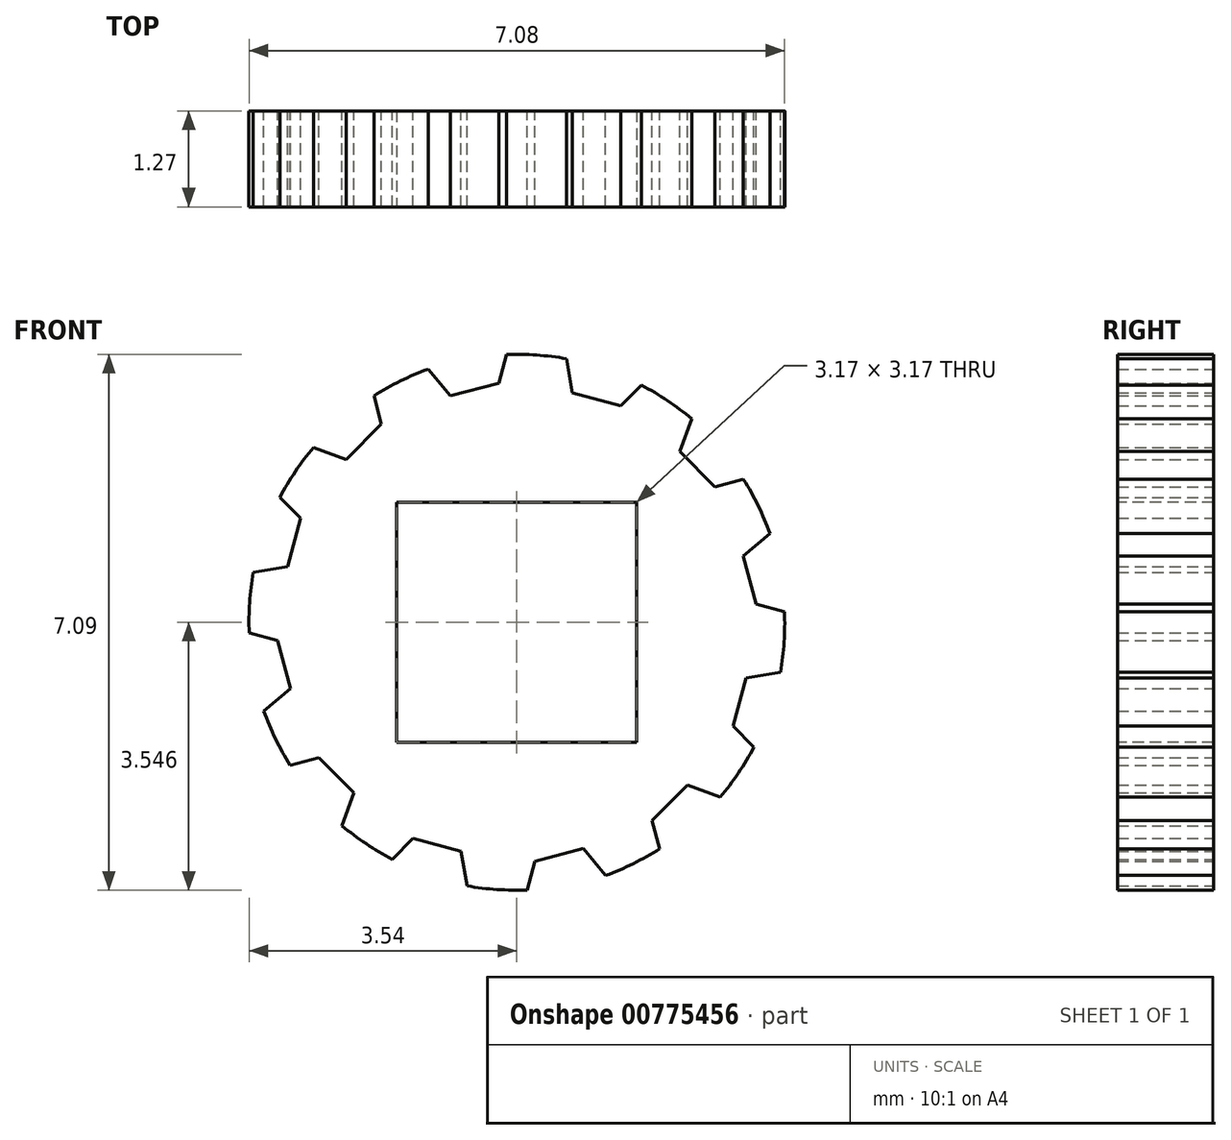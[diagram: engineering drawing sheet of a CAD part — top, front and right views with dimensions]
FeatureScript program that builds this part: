
annotation { "Feature Type Name" : "Feature", "Feature Type Description" : "" }
export const myFeature = defineFeature(function(context is Context, id is Id, definition is map)
    precondition{}
    {
        {
            var Q0;
            Q0=qCreatedBy(makeId("Front.planeOp"),FACE);
            var sketch = newSketch(context, id + "F0", { "sketchPlane" : qUnion([Q0])});
            skCircle(sketch, "E0", {"center": v(0, 0) * mm, "radius": 3.81 * mm});
            skLineSegment(sketch, "E1", {"start": v(3.81, 0) * mm, "end": v(3.81, -2.14) * mm});
            skLineSegment(sketch, "E2", {"start": v(3.81, 0) * mm, "end": v(3.81, 1.7) * mm});
            skLineSegment(sketch, "E3", {"start": v(3.81, -2.14) * mm, "end": v(3.81, 1.7) * mm});
            skLineSegment(sketch, "E4", {"start": v(0, 0) * mm, "end": v(4.56, 1.22) * mm});
            skLineSegment(sketch, "E5", {"start": v(0, 0) * mm, "end": v(5.89, -1.58) * mm});
            skLineSegment(sketch, "E6", {"start": v(0, 0) * mm, "end": v(6.8, 0.6) * mm});
            skLineSegment(sketch, "E7", {"start": v(0, 0) * mm, "end": v(7.02, -0.61) * mm});
            skLineSegment(sketch, "E8", {"start": v(3.81, 0.33) * mm, "end": v(4.14, 0.33) * mm});
            skLineSegment(sketch, "E9", {"start": v(3.81, -0.33) * mm, "end": v(4.23, -0.33) * mm});
            skLineSegment(sketch, "E10", {"start": v(3.08, 0.83) * mm, "end": v(3.16, 0.5) * mm});
            skLineSegment(sketch, "E11", {"start": v(3.08, 0.83) * mm, "end": v(3, 1.14) * mm});
            skLineSegment(sketch, "E12", {"start": v(3.16, 0.5) * mm, "end": v(3.81, 0.33) * mm});
            skLineSegment(sketch, "E13", {"start": v(3, 1.14) * mm, "end": v(3.6, 1.65) * mm});
            skLineSegment(sketch, "E14", {"start": v(3.81, 0.33) * mm, "end": v(3.6, 1.65) * mm});
            skLineSegment(sketch, "E15.1.0", {"start": v(2.15, 2.52) * mm, "end": v(2.43, 3.26) * mm});
            skLineSegment(sketch, "E15.1.1", {"start": v(3.27, 2.23) * mm, "end": v(2.43, 3.26) * mm});
            skLineSegment(sketch, "E15.1.2", {"start": v(2.39, 2.29) * mm, "end": v(2.15, 2.52) * mm});
            skLineSegment(sketch, "E15.1.3", {"start": v(2.39, 2.29) * mm, "end": v(2.62, 2.06) * mm});
            skLineSegment(sketch, "E15.1.4", {"start": v(2.62, 2.06) * mm, "end": v(3.27, 2.23) * mm});
            skCircle(sketch, "E15.1.5", {"center": v(0.13, 0.04) * mm, "radius": 3.81 * mm});
            skLineSegment(sketch, "E15.2.0", {"start": v(0.74, 3.3) * mm, "end": v(0.6, 4.07) * mm});
            skLineSegment(sketch, "E15.2.1", {"start": v(1.85, 3.6) * mm, "end": v(0.6, 4.07) * mm});
            skLineSegment(sketch, "E15.2.2", {"start": v(1.06, 3.21) * mm, "end": v(0.74, 3.3) * mm});
            skLineSegment(sketch, "E15.2.3", {"start": v(1.06, 3.21) * mm, "end": v(1.37, 3.13) * mm});
            skLineSegment(sketch, "E15.2.4", {"start": v(1.37, 3.13) * mm, "end": v(1.85, 3.6) * mm});
            skCircle(sketch, "E15.2.5", {"center": v(0.23, 0.13) * mm, "radius": 3.81 * mm});
            skLineSegment(sketch, "E15.3.0", {"start": v(-0.88, 3.26) * mm, "end": v(-1.38, 3.86) * mm});
            skLineSegment(sketch, "E15.3.1", {"start": v(-0.07, 4.08) * mm, "end": v(-1.38, 3.86) * mm});
            skLineSegment(sketch, "E15.3.2", {"start": v(-0.56, 3.35) * mm, "end": v(-0.88, 3.26) * mm});
            skLineSegment(sketch, "E15.3.3", {"start": v(-0.56, 3.35) * mm, "end": v(-0.24, 3.43) * mm});
            skLineSegment(sketch, "E15.3.4", {"start": v(-0.24, 3.43) * mm, "end": v(-0.07, 4.08) * mm});
            skCircle(sketch, "E15.3.5", {"center": v(0.27, 0.27) * mm, "radius": 3.81 * mm});
            skLineSegment(sketch, "E15.4.0", {"start": v(-2.26, 2.42) * mm, "end": v(-3, 2.7) * mm});
            skLineSegment(sketch, "E15.4.1", {"start": v(-1.96, 3.53) * mm, "end": v(-3, 2.7) * mm});
            skLineSegment(sketch, "E15.4.2", {"start": v(-2.02, 2.65) * mm, "end": v(-2.26, 2.42) * mm});
            skLineSegment(sketch, "E15.4.3", {"start": v(-2.02, 2.65) * mm, "end": v(-1.8, 2.89) * mm});
            skLineSegment(sketch, "E15.4.4", {"start": v(-1.8, 2.89) * mm, "end": v(-1.96, 3.53) * mm});
            skCircle(sketch, "E15.4.5", {"center": v(0.23, 0.4) * mm, "radius": 3.81 * mm});
            skLineSegment(sketch, "E15.5.0", {"start": v(-3.03, 1) * mm, "end": v(-3.8, 0.87) * mm});
            skLineSegment(sketch, "E15.5.1", {"start": v(-3.33, 2.11) * mm, "end": v(-3.8, 0.87) * mm});
            skLineSegment(sketch, "E15.5.2", {"start": v(-2.95, 1.32) * mm, "end": v(-3.03, 1) * mm});
            skLineSegment(sketch, "E15.5.3", {"start": v(-2.95, 1.32) * mm, "end": v(-2.86, 1.64) * mm});
            skLineSegment(sketch, "E15.5.4", {"start": v(-2.86, 1.64) * mm, "end": v(-3.33, 2.11) * mm});
            skCircle(sketch, "E15.5.5", {"center": v(0.13, 0.5) * mm, "radius": 3.81 * mm});
            skLineSegment(sketch, "E15.6.0", {"start": v(-3, -0.61) * mm, "end": v(-3.6, -1.11) * mm});
            skLineSegment(sketch, "E15.6.1", {"start": v(-3.81, 0.2) * mm, "end": v(-3.6, -1.11) * mm});
            skLineSegment(sketch, "E15.6.2", {"start": v(-3.08, -0.3) * mm, "end": v(-3, -0.61) * mm});
            skLineSegment(sketch, "E15.6.3", {"start": v(-3.08, -0.3) * mm, "end": v(-3.16, 0.03) * mm});
            skLineSegment(sketch, "E15.6.4", {"start": v(-3.16, 0.03) * mm, "end": v(-3.81, 0.2) * mm});
            skCircle(sketch, "E15.6.5", {"center": v(0, 0.53) * mm, "radius": 3.81 * mm});
            skLineSegment(sketch, "E15.7.0", {"start": v(-2.15, -2) * mm, "end": v(-2.43, -2.73) * mm});
            skLineSegment(sketch, "E15.7.1", {"start": v(-3.27, -1.7) * mm, "end": v(-2.43, -2.73) * mm});
            skLineSegment(sketch, "E15.7.2", {"start": v(-2.39, -1.76) * mm, "end": v(-2.15, -2) * mm});
            skLineSegment(sketch, "E15.7.3", {"start": v(-2.39, -1.76) * mm, "end": v(-2.62, -1.52) * mm});
            skLineSegment(sketch, "E15.7.4", {"start": v(-2.62, -1.52) * mm, "end": v(-3.27, -1.7) * mm});
            skCircle(sketch, "E15.7.5", {"center": v(-0.13, 0.5) * mm, "radius": 3.81 * mm});
            skLineSegment(sketch, "E15.8.0", {"start": v(-0.74, -2.77) * mm, "end": v(-0.6, -3.54) * mm});
            skLineSegment(sketch, "E15.8.1", {"start": v(-1.85, -3.07) * mm, "end": v(-0.6, -3.54) * mm});
            skLineSegment(sketch, "E15.8.2", {"start": v(-1.06, -2.68) * mm, "end": v(-0.74, -2.77) * mm});
            skLineSegment(sketch, "E15.8.3", {"start": v(-1.06, -2.68) * mm, "end": v(-1.37, -2.6) * mm});
            skLineSegment(sketch, "E15.8.4", {"start": v(-1.37, -2.6) * mm, "end": v(-1.85, -3.07) * mm});
            skCircle(sketch, "E15.8.5", {"center": v(-0.23, 0.4) * mm, "radius": 3.81 * mm});
            skLineSegment(sketch, "E15.9.0", {"start": v(0.88, -2.73) * mm, "end": v(1.38, -3.33) * mm});
            skLineSegment(sketch, "E15.9.1", {"start": v(0.07, -3.54) * mm, "end": v(1.38, -3.33) * mm});
            skLineSegment(sketch, "E15.9.2", {"start": v(0.56, -2.81) * mm, "end": v(0.88, -2.73) * mm});
            skLineSegment(sketch, "E15.9.3", {"start": v(0.56, -2.81) * mm, "end": v(0.24, -2.9) * mm});
            skLineSegment(sketch, "E15.9.4", {"start": v(0.24, -2.9) * mm, "end": v(0.07, -3.54) * mm});
            skCircle(sketch, "E15.9.5", {"center": v(-0.27, 0.27) * mm, "radius": 3.81 * mm});
            skLineSegment(sketch, "E15.10.0", {"start": v(2.26, -1.89) * mm, "end": v(3, -2.16) * mm});
            skLineSegment(sketch, "E15.10.1", {"start": v(1.96, -3) * mm, "end": v(3, -2.16) * mm});
            skLineSegment(sketch, "E15.10.2", {"start": v(2.02, -2.12) * mm, "end": v(2.26, -1.89) * mm});
            skLineSegment(sketch, "E15.10.3", {"start": v(2.02, -2.12) * mm, "end": v(1.8, -2.35) * mm});
            skLineSegment(sketch, "E15.10.4", {"start": v(1.8, -2.35) * mm, "end": v(1.96, -3) * mm});
            skCircle(sketch, "E15.10.5", {"center": v(-0.23, 0.13) * mm, "radius": 3.81 * mm});
            skLineSegment(sketch, "E15.11.0", {"start": v(3.03, -0.47) * mm, "end": v(3.8, -0.34) * mm});
            skLineSegment(sketch, "E15.11.1", {"start": v(3.33, -1.58) * mm, "end": v(3.8, -0.34) * mm});
            skLineSegment(sketch, "E15.11.2", {"start": v(2.95, -0.79) * mm, "end": v(3.03, -0.47) * mm});
            skLineSegment(sketch, "E15.11.3", {"start": v(2.95, -0.79) * mm, "end": v(2.86, -1.1) * mm});
            skLineSegment(sketch, "E15.11.4", {"start": v(2.86, -1.1) * mm, "end": v(3.33, -1.58) * mm});
            skCircle(sketch, "E15.11.5", {"center": v(-0.13, 0.04) * mm, "radius": 3.81 * mm});
            skPoint(sketch, "E15.center", {"position": v(0, 0.27) * mm});
            skLineSegment(sketch, "E16", {"start": v(3.27, 2.23) * mm, "end": v(3.6, 1.65) * mm});
            skLineSegment(sketch, "E17", {"start": v(1.85, 3.6) * mm, "end": v(2.43, 3.26) * mm});
            skLineSegment(sketch, "E18", {"start": v(-1.38, 3.86) * mm, "end": v(-0.07, 4.08) * mm});
            skLineSegment(sketch, "E19", {"start": v(-1.96, 3.53) * mm, "end": v(-1.38, 3.86) * mm});
            skLineSegment(sketch, "E20", {"start": v(-0.07, 4.08) * mm, "end": v(0.6, 4.07) * mm});
            skLineSegment(sketch, "E21", {"start": v(-3, 2.7) * mm, "end": v(-3.33, 2.11) * mm});
            skLineSegment(sketch, "E22", {"start": v(-3.8, 0.87) * mm, "end": v(-3.81, 0.2) * mm});
            skLineSegment(sketch, "E23", {"start": v(-3.6, -1.11) * mm, "end": v(-3.27, -1.7) * mm});
            skLineSegment(sketch, "E24", {"start": v(-2.43, -2.73) * mm, "end": v(-1.85, -3.07) * mm});
            skLineSegment(sketch, "E25", {"start": v(-0.6, -3.54) * mm, "end": v(0.07, -3.54) * mm});
            skLineSegment(sketch, "E26", {"start": v(1.38, -3.33) * mm, "end": v(1.96, -3) * mm});
            skLineSegment(sketch, "E27", {"start": v(3, -2.16) * mm, "end": v(3.33, -1.58) * mm});
            skLineSegment(sketch, "E28", {"start": v(3.8, -0.34) * mm, "end": v(3.81, 0.33) * mm});
            skSolve(sketch);
        }
        {
            var Q0;
            {var subQ49=sQuery(id+"F0.wireOp",EDGE,"E11");Q0=makeQuery(id+"F0.imprint","IMPRINT",FACE,{"disambiguationData":[TD([[makeQuery(id+"F0.imprint","IMPRINT",EDGE,{"derivedFrom":subQ49}),1.0]])]});}
            var Q1;
            {var subQ0=sQuery(id+"F0.wireOp",EDGE,"E15.11.2");Q1=makeQuery(id+"F0.imprint","IMPRINT",FACE,{"disambiguationData":[TD([[makeQuery(id+"F0.imprint","IMPRINT",EDGE,{"derivedFrom":subQ0}),1.0]])]});}
            var Q2;
            {var subQ1=sQuery(id+"F0.wireOp",EDGE,"E6");var subQ3=sQuery(id+"F0.wireOp",EDGE,"E15.9.5");var subQ4=makeQuery(id+"F0.imprint","INTERSECT",VERTEX,{"derivedFrom":[subQ1,subQ3]});Q2=makeQuery(id+"F0.imprint","IMPRINT",FACE,{"disambiguationData":[TD([[makeQuery(id+"F0.imprint","IMPRINT",EDGE,{"disambiguationData":[TD([[subQ4,1.0]])],"derivedFrom":subQ3}),1.0]])]});}
            var Q3;
            {var subQ1=sQuery(id+"F0.wireOp",EDGE,"E10");Q3=makeQuery(id+"F0.imprint","IMPRINT",FACE,{"disambiguationData":[TD([[makeQuery(id+"F0.imprint","IMPRINT",EDGE,{"derivedFrom":subQ1}),-1.0]])]});}
            extrude(context, id + "F1", {"entities" : qUnion([Q0, Q1, Q2, Q3]), "depth" : 1.27 * mm, "offsetDistance" : 25.4 * mm});
        }
        {
            var Q0;
            Q0=makeQuery(id+"F1.opExtrude","CAP_FACE",FACE,{"disambiguationData":[OSD([sQuery(id+"F0.wireOp",EDGE,"E0"),sQuery(id+"F0.wireOp",EDGE,"E10"),sQuery(id+"F0.wireOp",EDGE,"E11"),sQuery(id+"F0.wireOp",EDGE,"E12"),sQuery(id+"F0.wireOp",EDGE,"E13"),sQuery(id+"F0.wireOp",EDGE,"E15.1.0"),sQuery(id+"F0.wireOp",EDGE,"E15.1.2"),sQuery(id+"F0.wireOp",EDGE,"E15.1.3"),sQuery(id+"F0.wireOp",EDGE,"E15.1.4"),sQuery(id+"F0.wireOp",EDGE,"E15.1.5"),sQuery(id+"F0.wireOp",EDGE,"E15.2.0"),sQuery(id+"F0.wireOp",EDGE,"E15.2.2"),sQuery(id+"F0.wireOp",EDGE,"E15.2.3"),sQuery(id+"F0.wireOp",EDGE,"E15.2.4"),sQuery(id+"F0.wireOp",EDGE,"E15.2.5"),sQuery(id+"F0.wireOp",EDGE,"E15.3.0"),sQuery(id+"F0.wireOp",EDGE,"E15.3.2"),sQuery(id+"F0.wireOp",EDGE,"E15.3.3"),sQuery(id+"F0.wireOp",EDGE,"E15.3.4"),sQuery(id+"F0.wireOp",EDGE,"E15.3.5"),sQuery(id+"F0.wireOp",EDGE,"E15.4.0"),sQuery(id+"F0.wireOp",EDGE,"E15.4.2"),sQuery(id+"F0.wireOp",EDGE,"E15.4.3"),sQuery(id+"F0.wireOp",EDGE,"E15.4.4"),sQuery(id+"F0.wireOp",EDGE,"E15.4.5"),sQuery(id+"F0.wireOp",EDGE,"E15.5.0"),sQuery(id+"F0.wireOp",EDGE,"E15.5.2"),sQuery(id+"F0.wireOp",EDGE,"E15.5.3"),sQuery(id+"F0.wireOp",EDGE,"E15.5.4"),sQuery(id+"F0.wireOp",EDGE,"E15.5.5"),sQuery(id+"F0.wireOp",EDGE,"E15.6.0"),sQuery(id+"F0.wireOp",EDGE,"E15.6.2"),sQuery(id+"F0.wireOp",EDGE,"E15.6.3"),sQuery(id+"F0.wireOp",EDGE,"E15.6.4"),sQuery(id+"F0.wireOp",EDGE,"E15.6.5"),sQuery(id+"F0.wireOp",EDGE,"E15.7.0"),sQuery(id+"F0.wireOp",EDGE,"E15.7.2"),sQuery(id+"F0.wireOp",EDGE,"E15.7.3"),sQuery(id+"F0.wireOp",EDGE,"E15.7.4"),sQuery(id+"F0.wireOp",EDGE,"E15.7.5"),sQuery(id+"F0.wireOp",EDGE,"E15.8.0"),sQuery(id+"F0.wireOp",EDGE,"E15.8.2"),sQuery(id+"F0.wireOp",EDGE,"E15.8.3"),sQuery(id+"F0.wireOp",EDGE,"E15.8.4"),sQuery(id+"F0.wireOp",EDGE,"E15.8.5"),sQuery(id+"F0.wireOp",EDGE,"E15.9.0"),sQuery(id+"F0.wireOp",EDGE,"E15.9.2"),sQuery(id+"F0.wireOp",EDGE,"E15.9.3"),sQuery(id+"F0.wireOp",EDGE,"E15.9.4"),sQuery(id+"F0.wireOp",EDGE,"E15.9.5"),sQuery(id+"F0.wireOp",EDGE,"E15.10.0"),sQuery(id+"F0.wireOp",EDGE,"E15.10.2"),sQuery(id+"F0.wireOp",EDGE,"E15.10.3"),sQuery(id+"F0.wireOp",EDGE,"E15.10.4"),sQuery(id+"F0.wireOp",EDGE,"E15.10.5"),sQuery(id+"F0.wireOp",EDGE,"E15.11.0"),sQuery(id+"F0.wireOp",EDGE,"E15.11.2"),sQuery(id+"F0.wireOp",EDGE,"E15.11.3"),sQuery(id+"F0.wireOp",EDGE,"E15.11.4"),sQuery(id+"F0.wireOp",EDGE,"E15.11.5")])],"isStart":false});
            var sketch = newSketch(context, id + "F2", { "sketchPlane" : qUnion([Q0])});
            skPoint(sketch, "E29.middle", {"position": v(0, 0) * mm});
            skLineSegment(sketch, "E30.0.0", {"start": v(2.86, -1.1) * mm, "end": v(3.03, -0.47) * mm});
            skLineSegment(sketch, "E30.0.1", {"start": v(3.03, -0.47) * mm, "end": v(3.49, -0.4) * mm});
            skArc(sketch, "E30.0.2", {"start": v(3.49, -0.4) * mm, "mid": v(3.53, 0) * mm, "end": v(3.54, 0.4) * mm});
            skLineSegment(sketch, "E30.0.3", {"start": v(3.54, 0.4) * mm, "end": v(3.16, 0.5) * mm});
            skLineSegment(sketch, "E30.0.4", {"start": v(3.16, 0.5) * mm, "end": v(3, 1.14) * mm});
            skLineSegment(sketch, "E30.0.5", {"start": v(3, 1.14) * mm, "end": v(3.35, 1.44) * mm});
            skArc(sketch, "E30.0.6", {"start": v(3.35, 1.44) * mm, "mid": v(3.2, 1.8) * mm, "end": v(3, 2.16) * mm});
            skLineSegment(sketch, "E30.0.7", {"start": v(3, 2.16) * mm, "end": v(2.62, 2.06) * mm});
            skLineSegment(sketch, "E30.0.8", {"start": v(2.62, 2.06) * mm, "end": v(2.15, 2.52) * mm});
            skLineSegment(sketch, "E30.0.9", {"start": v(2.15, 2.52) * mm, "end": v(2.31, 2.96) * mm});
            skArc(sketch, "E30.0.10", {"start": v(2.31, 2.96) * mm, "mid": v(2, 3.2) * mm, "end": v(1.65, 3.4) * mm});
            skLineSegment(sketch, "E30.0.11", {"start": v(1.65, 3.4) * mm, "end": v(1.37, 3.13) * mm});
            skLineSegment(sketch, "E30.0.12", {"start": v(1.37, 3.13) * mm, "end": v(0.74, 3.3) * mm});
            skLineSegment(sketch, "E30.0.13", {"start": v(0.74, 3.3) * mm, "end": v(0.66, 3.75) * mm});
            skArc(sketch, "E30.0.14", {"start": v(0.66, 3.75) * mm, "mid": v(0.26, 3.8) * mm, "end": v(-0.14, 3.8) * mm});
            skLineSegment(sketch, "E30.0.15", {"start": v(-0.14, 3.8) * mm, "end": v(-0.24, 3.43) * mm});
            skLineSegment(sketch, "E30.0.16", {"start": v(-0.24, 3.43) * mm, "end": v(-0.88, 3.26) * mm});
            skLineSegment(sketch, "E30.0.17", {"start": v(-0.88, 3.26) * mm, "end": v(-1.17, 3.61) * mm});
            skArc(sketch, "E30.0.18", {"start": v(-1.17, 3.61) * mm, "mid": v(-1.54, 3.46) * mm, "end": v(-1.9, 3.26) * mm});
            skLineSegment(sketch, "E30.0.19", {"start": v(-1.9, 3.26) * mm, "end": v(-1.8, 2.89) * mm});
            skLineSegment(sketch, "E30.0.20", {"start": v(-1.8, 2.89) * mm, "end": v(-2.26, 2.42) * mm});
            skLineSegment(sketch, "E30.0.21", {"start": v(-2.26, 2.42) * mm, "end": v(-2.7, 2.58) * mm});
            skArc(sketch, "E30.0.22", {"start": v(-2.7, 2.58) * mm, "mid": v(-2.93, 2.26) * mm, "end": v(-3.14, 1.92) * mm});
            skLineSegment(sketch, "E30.0.23", {"start": v(-3.14, 1.92) * mm, "end": v(-2.86, 1.64) * mm});
            skLineSegment(sketch, "E30.0.24", {"start": v(-2.86, 1.64) * mm, "end": v(-3.03, 1) * mm});
            skLineSegment(sketch, "E30.0.25", {"start": v(-3.03, 1) * mm, "end": v(-3.49, 0.92) * mm});
            skArc(sketch, "E30.0.26", {"start": v(-3.49, 0.92) * mm, "mid": v(-3.53, 0.53) * mm, "end": v(-3.54, 0.13) * mm});
            skLineSegment(sketch, "E30.0.27", {"start": v(-3.54, 0.13) * mm, "end": v(-3.16, 0.03) * mm});
            skLineSegment(sketch, "E30.0.28", {"start": v(-3.16, 0.03) * mm, "end": v(-3, -0.61) * mm});
            skLineSegment(sketch, "E30.0.29", {"start": v(-3, -0.61) * mm, "end": v(-3.35, -0.9) * mm});
            skArc(sketch, "E30.0.30", {"start": v(-3.35, -0.9) * mm, "mid": v(-3.2, -1.28) * mm, "end": v(-3, -1.63) * mm});
            skLineSegment(sketch, "E30.0.31", {"start": v(-3, -1.63) * mm, "end": v(-2.62, -1.52) * mm});
            skLineSegment(sketch, "E30.0.32", {"start": v(-2.62, -1.52) * mm, "end": v(-2.15, -2) * mm});
            skLineSegment(sketch, "E30.0.33", {"start": v(-2.15, -2) * mm, "end": v(-2.31, -2.42) * mm});
            skArc(sketch, "E30.0.34", {"start": v(-2.31, -2.42) * mm, "mid": v(-2, -2.66) * mm, "end": v(-1.65, -2.87) * mm});
            skLineSegment(sketch, "E30.0.35", {"start": v(-1.65, -2.87) * mm, "end": v(-1.37, -2.6) * mm});
            skLineSegment(sketch, "E30.0.36", {"start": v(-1.37, -2.6) * mm, "end": v(-0.74, -2.77) * mm});
            skLineSegment(sketch, "E30.0.37", {"start": v(-0.74, -2.77) * mm, "end": v(-0.66, -3.22) * mm});
            skArc(sketch, "E30.0.38", {"start": v(-0.66, -3.22) * mm, "mid": v(-0.26, -3.27) * mm, "end": v(0.14, -3.28) * mm});
            skLineSegment(sketch, "E30.0.39", {"start": v(0.14, -3.28) * mm, "end": v(0.24, -2.9) * mm});
            skLineSegment(sketch, "E30.0.40", {"start": v(0.24, -2.9) * mm, "end": v(0.88, -2.73) * mm});
            skLineSegment(sketch, "E30.0.41", {"start": v(0.88, -2.73) * mm, "end": v(1.17, -3.08) * mm});
            skArc(sketch, "E30.0.42", {"start": v(1.17, -3.08) * mm, "mid": v(1.54, -2.93) * mm, "end": v(1.9, -2.73) * mm});
            skLineSegment(sketch, "E30.0.43", {"start": v(1.9, -2.73) * mm, "end": v(1.8, -2.35) * mm});
            skLineSegment(sketch, "E30.0.44", {"start": v(1.8, -2.35) * mm, "end": v(2.26, -1.89) * mm});
            skLineSegment(sketch, "E30.0.45", {"start": v(2.26, -1.89) * mm, "end": v(2.7, -2.05) * mm});
            skArc(sketch, "E30.0.46", {"start": v(2.7, -2.05) * mm, "mid": v(2.93, -1.73) * mm, "end": v(3.14, -1.38) * mm});
            skLineSegment(sketch, "E30.0.47", {"start": v(3.14, -1.38) * mm, "end": v(2.86, -1.1) * mm});
            skLineSegment(sketch, "E31.bottom", {"start": v(-1.59, -1.32) * mm, "end": v(1.59, -1.32) * mm});
            skLineSegment(sketch, "E31.top", {"start": v(-1.59, 1.85) * mm, "end": v(1.59, 1.85) * mm});
            skLineSegment(sketch, "E31.left", {"start": v(-1.59, -1.32) * mm, "end": v(-1.59, 1.85) * mm});
            skLineSegment(sketch, "E31.right", {"start": v(1.59, -1.32) * mm, "end": v(1.59, 1.85) * mm});
            skPoint(sketch, "E31.middle", {"position": v(0, 0.27) * mm});
            skSolve(sketch);
        }
        {
            var Q0;
            Q0=makeQuery(id+"F2.imprint","IMPRINT",FACE,{"disambiguationData":[TD([[makeQuery(id+"F2.imprint","IMPRINT",EDGE,{"derivedFrom":sQuery(id+"F2.wireOp",EDGE,"E31.bottom")}),1.0]])]});
            extrude(context, id + "F3", {"entities" : qUnion([Q0]), "operationType" : NewBodyOperationType.REMOVE, "oppositeDirection" : true, "depth" : 25.4 * mm, "offsetDistance" : 25.4 * mm});
        }
    });
